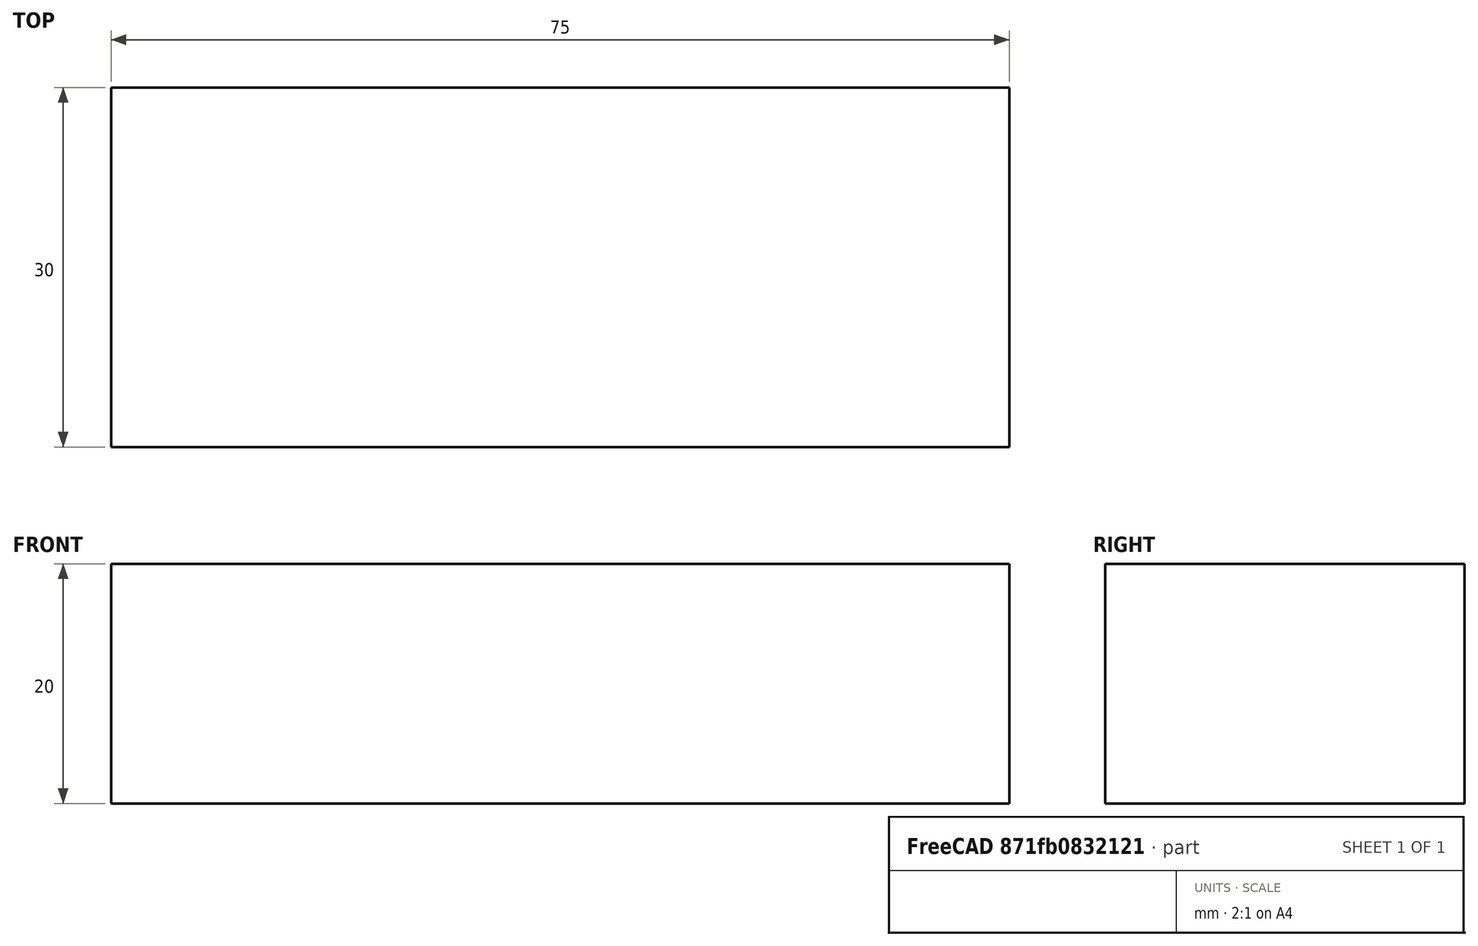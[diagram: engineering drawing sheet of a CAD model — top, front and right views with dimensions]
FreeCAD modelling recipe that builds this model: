
FCSTD DOCUMENT  (FreeCAD 0.18.4R)
Label: gripper-body
License: All rights reserved
LicenseURL: http://en.wikipedia.org/wiki/All_rights_reserved
objects: Sketcher::SketchObject×1, PartDesign::Pad×1, PartDesign::Body×1
note: 4 computed .brp shape members not serialized (recipe doc carries the construction recipe); baked Part::Feature solids carry a one-line shape summary decoded from their .brp

FEATURE [Sketcher::SketchObject] Sketch
  MapMode = 5
  Placement = pos=(0,0,0) rot=(1,0,0;1.5708rad)
  Support = -> [XZ_Plane]
  sketch-geometry (4):
    g0: LineSegment StartX=-37.5 StartY=10 StartZ=0 EndX=37.5 EndY=10 EndZ=0
    g1: LineSegment StartX=37.5 StartY=10 StartZ=0 EndX=37.5 EndY=-10 EndZ=0
    g2: LineSegment StartX=37.5 StartY=-10 StartZ=0 EndX=-37.5 EndY=-10 EndZ=0
    g3: LineSegment StartX=-37.5 StartY=-10 StartZ=0 EndX=-37.5 EndY=10 EndZ=0
  constraints (10):
    c: Coincident(g0,g1)
    c: Coincident(g1,g2)
    c: Coincident(g2,g3)
    c: Coincident(g3,g0)
    c: Horizontal(g0)
    c: Horizontal(g2)
    c: Vertical(g1)
    c: Vertical(g3)
    c: DistanceX(g0,g0) = 75
    c: DistanceY(g3,g3) = 20
FEATURE [PartDesign::Pad] Pad
  Length = 15
  Length2 = 15
  Midplane = true
  Placement = pos=(0,0,0) rot=(1,0,0;1.5708rad)
  Profile = -> Sketch
  Type = 4
FEATURE [PartDesign::Body] Body
  Group = -> [Sketch,Pad]
  Origin = -> Origin
  Tip = -> Pad
